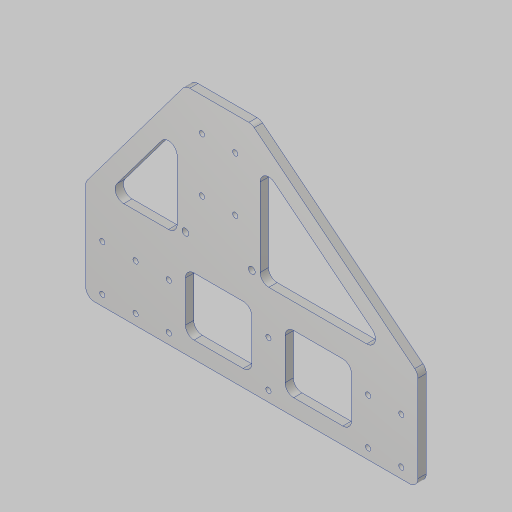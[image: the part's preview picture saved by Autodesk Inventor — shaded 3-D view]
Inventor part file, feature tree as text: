
AUTODESK INVENTOR PART (.ipt)
format: ipt  version: 2023.5 (Build 275446000, 446)  size: 252,416 bytes
history: native  units: in
note: dims shown in document units (in); Inventor stores cm internally (conversion verified against a paired STEP export)
features: sketch x2, extrude x2, hole x2, fillet x2, projected_geometry x1
ambient origin geometry x8: Origin, YZ Plane, XZ Plane, XY Plane, X Axis, Y Axis, Z Axis, Center Point
bodies: Solid1 (feature_tree)
feature tree (9):
  sketch  "Sketch1"  dims[d0=2.0in d1=8.0in]
  extrude  "Extrusion1"  Depth=8.0in
  hole  "Hole1"  [1 undecoded]
  fillet  "Fillet1"  Radius=5.0in
  extrude  "Extrusion2"  Depth=0.5in
  fillet  "Fillet2"  Radius=0.5in
  hole  "Hole2"  [1 undecoded]
  sketch  "Sketch2"  dims[d2=10.0in d3=3.0in d4=5.0in d5=0.5in d6=0.5in d7=0.375in d8=0.125in d9=0.375in d10=3.937in d12=1.0in d13=0.3937in d15=1.0in d17=1.0in d18=1.375in d19=1.0in d20=0.5in d21=0.375in d22=0.375in d23=0.25in d24=0.0in d25=0.156in d26=0.38in d27=0.385in d28=0.25in d29=0.5635in d30=1.0in d31=0.8108in d32=4.375in d33=1.625in d34=0.26in d35=0.5in d36=0.5in d37=0.375in d38=2.0in d39=1.375in d40=0.25in d41=0.25in d44=0.5in d45=0.75in d46=1.0in d47=0.0in d48=0.26in d49=0.5in d50=0.5in d51=0.5in d52=0.5in d53=0.5in d54=0.5in d55=0.201in d56=0.38in d57=0.385in d58=0.25in d59=0.5635in d60=1.0in d61=0.8108in]
  projected_geometry  "Project Cut Edges1"
note: 2 required parameter values undecoded (feature->parameter linkage not recoverable at this tier; creation-order binding heuristic only, values carry confidence <= 0.55)
